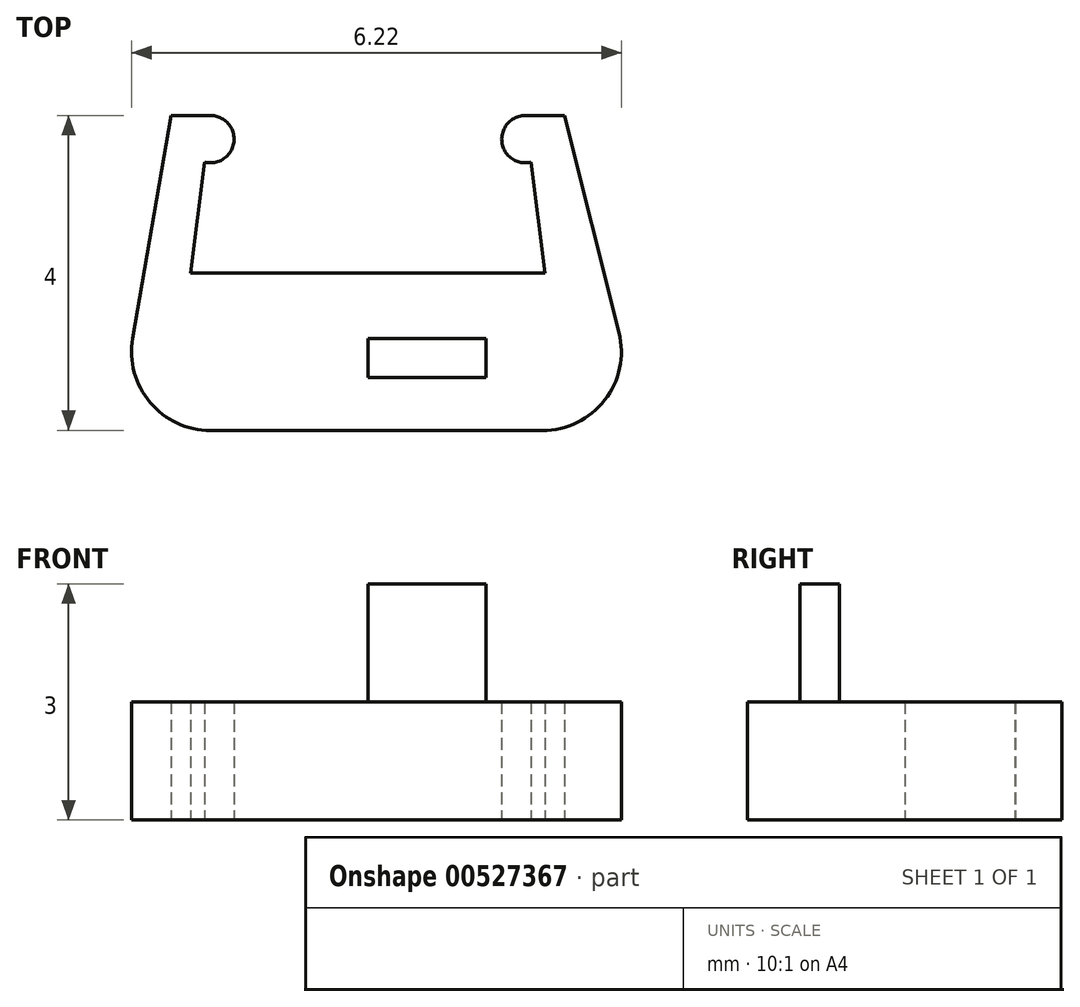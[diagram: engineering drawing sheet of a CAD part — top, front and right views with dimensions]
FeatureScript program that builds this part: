
annotation { "Feature Type Name" : "Feature", "Feature Type Description" : "" }
export const myFeature = defineFeature(function(context is Context, id is Id, definition is map)
    precondition{}
    {
        {
            var Q0;
            Q0=qCreatedBy(makeId("Top.planeOp"),FACE);
            var sketch = newSketch(context, id + "F0", { "sketchPlane" : qUnion([Q0])});
            skLineSegment(sketch, "E0", {"start": v(19.49, 16.65) * mm, "end": v(19.31, 15.24) * mm});
            skLineSegment(sketch, "E1", {"start": v(19.31, 15.24) * mm, "end": v(23.81, 15.24) * mm});
            skLineSegment(sketch, "E2", {"start": v(23.81, 15.24) * mm, "end": v(23.63, 16.65) * mm});
            skLineSegment(sketch, "E3", {"start": v(23.56, 17.24) * mm, "end": v(24.06, 17.24) * mm});
            skLineSegment(sketch, "E4", {"start": v(24.06, 17.24) * mm, "end": v(24.75, 14.48) * mm});
            skLineSegment(sketch, "E5", {"start": v(23.78, 13.24) * mm, "end": v(19.56, 13.24) * mm});
            skLineSegment(sketch, "E6", {"start": v(18.57, 14.4) * mm, "end": v(19.06, 17.24) * mm});
            skLineSegment(sketch, "E7", {"start": v(19.06, 17.24) * mm, "end": v(19.56, 17.24) * mm});
            skPoint(sketch, "E8.visualSharp", {"position": v(25.06, 13.24) * mm});
            skArc(sketch, "E8.filletArc", {"start": v(23.78, 13.24) * mm, "mid": v(24.57, 13.62) * mm, "end": v(24.75, 14.48) * mm});
            skPoint(sketch, "E9.visualSharp", {"position": v(18.37, 13.24) * mm});
            skArc(sketch, "E9.filletArc", {"start": v(18.57, 14.4) * mm, "mid": v(18.8, 13.6) * mm, "end": v(19.56, 13.24) * mm});
            skLineSegment(sketch, "E10", {"start": v(23.56, 17.24) * mm, "end": v(23.56, 16.94) * mm, "construction": true});
            skArc(sketch, "E11", {"start": v(23.56, 17.24) * mm, "mid": v(23.26, 16.9) * mm, "end": v(23.63, 16.65) * mm});
            skLineSegment(sketch, "E12", {"start": v(21.56, 15.24) * mm, "end": v(21.56, 16) * mm, "construction": true});
            skPoint(sketch, "E12.endSnap0", {"position": v(21.56, 15.24) * mm});
            skArc(sketch, "E13.MirrorC", {"start": v(19.56, 17.24) * mm, "mid": v(19.86, 16.9) * mm, "end": v(19.49, 16.65) * mm});
            skSolve(sketch);
        }
        {
            var Q0;
            Q0 = qSketchRegion(id + "F0", true);
            extrude(context, id + "F1", {"entities" : qUnion([Q0]), "depth" : 1.5 * mm, "offsetDistance" : 25 * mm});
        }
        {
            var Q0;
            Q0=makeQuery(id+"F1.opExtrude","CAP_FACE",FACE,{"disambiguationData":[OSD([sQuery(id+"F0.wireOp",EDGE,"E0"),sQuery(id+"F0.wireOp",EDGE,"E1"),sQuery(id+"F0.wireOp",EDGE,"E2"),sQuery(id+"F0.wireOp",EDGE,"E3"),sQuery(id+"F0.wireOp",EDGE,"E4"),sQuery(id+"F0.wireOp",EDGE,"E5"),sQuery(id+"F0.wireOp",EDGE,"E6"),sQuery(id+"F0.wireOp",EDGE,"E7"),sQuery(id+"F0.wireOp",EDGE,"E8.filletArc"),sQuery(id+"F0.wireOp",EDGE,"E9.filletArc"),sQuery(id+"F0.wireOp",EDGE,"E11"),sQuery(id+"F0.wireOp",EDGE,"E13.MirrorC")])],"isStart":false});
            var sketch = newSketch(context, id + "F2", { "sketchPlane" : qUnion([Q0])});
            skPoint(sketch, "E14.firstSnap0", {"position": v(21.56, 15.24) * mm});
            skLineSegment(sketch, "E14.bottom", {"start": v(21.56, 14.4) * mm, "end": v(23.06, 14.4) * mm});
            skLineSegment(sketch, "E14.top", {"start": v(21.56, 13.9) * mm, "end": v(23.06, 13.9) * mm});
            skLineSegment(sketch, "E14.left", {"start": v(21.56, 14.4) * mm, "end": v(21.56, 13.9) * mm});
            skLineSegment(sketch, "E14.right", {"start": v(23.06, 14.4) * mm, "end": v(23.06, 13.9) * mm});
            skSolve(sketch);
        }
        {
            var Q0;
            Q0 = qSketchRegion(id + "F2", true);
            extrude(context, id + "F3", {"entities" : qUnion([Q0]), "operationType" : NewBodyOperationType.ADD, "depth" : 1.5 * mm, "offsetDistance" : 25 * mm});
        }
    });
